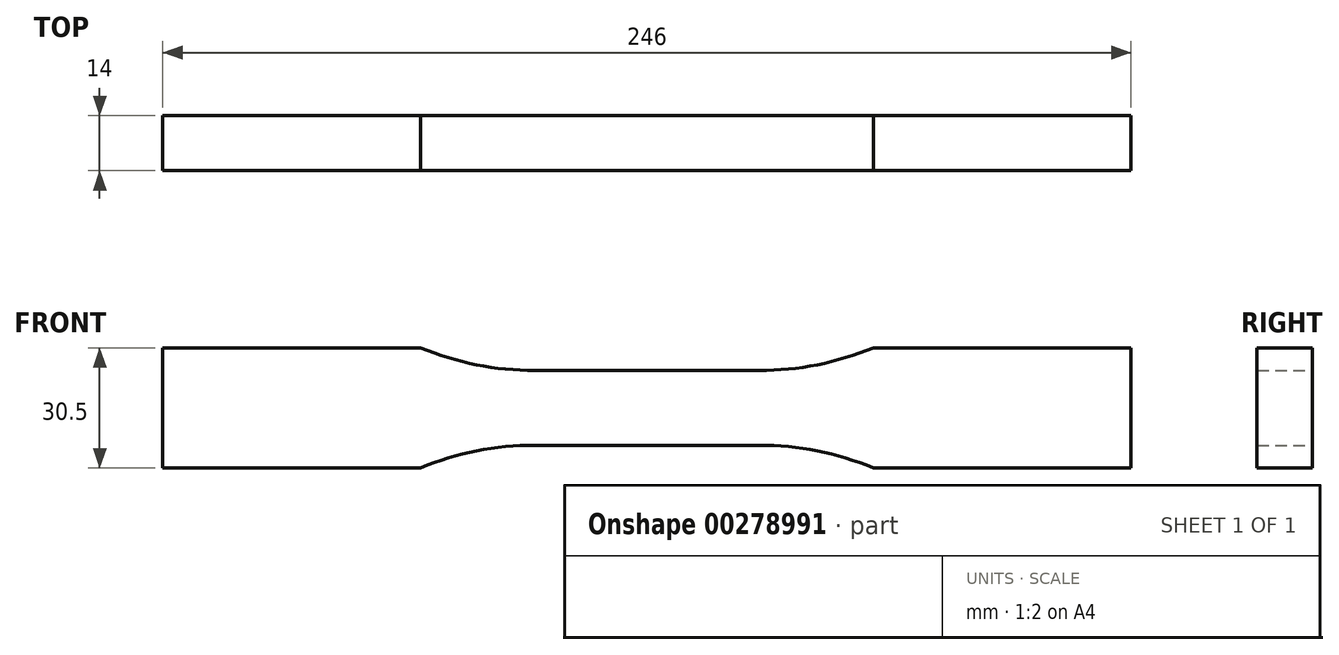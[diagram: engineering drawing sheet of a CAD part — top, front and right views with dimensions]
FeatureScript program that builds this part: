
annotation { "Feature Type Name" : "Feature", "Feature Type Description" : "" }
export const myFeature = defineFeature(function(context is Context, id is Id, definition is map)
    precondition{}
    {
        {
            var Q0;
            Q0=qCreatedBy(makeId("Front.planeOp"),FACE);
            var sketch = newSketch(context, id + "F0", { "sketchPlane" : qUnion([Q0])});
            skLineSegment(sketch, "E0", {"start": v(0, 9.5) * mm, "end": v(28.5, 9.5) * mm});
            skArc(sketch, "E1", {"start": v(28.5, 9.5) * mm, "mid": v(43.28, 10.95) * mm, "end": v(57.5, 15.25) * mm});
            skLineSegment(sketch, "E2", {"start": v(57.5, 15.25) * mm, "end": v(123, 15.25) * mm});
            skLineSegment(sketch, "E3.MirrorCS", {"start": v(-57.5, 15.25) * mm, "end": v(-123, 15.25) * mm});
            skLineSegment(sketch, "E4.MirrorCS", {"start": v(0, 9.5) * mm, "end": v(-28.5, 9.5) * mm});
            skArc(sketch, "E5.MirrorCS", {"start": v(-28.5, 9.5) * mm, "mid": v(-43.28, 10.95) * mm, "end": v(-57.5, 15.25) * mm});
            skArc(sketch, "E6.MirrorCS", {"start": v(-28.5, -9.5) * mm, "mid": v(-43.28, -10.95) * mm, "end": v(-57.5, -15.25) * mm});
            skLineSegment(sketch, "E7.MirrorCS", {"start": v(0, -9.5) * mm, "end": v(28.5, -9.5) * mm});
            skArc(sketch, "E8.MirrorCS", {"start": v(28.5, -9.5) * mm, "mid": v(43.28, -10.95) * mm, "end": v(57.5, -15.25) * mm});
            skLineSegment(sketch, "E9.MirrorCS", {"start": v(-57.5, -15.25) * mm, "end": v(-123, -15.25) * mm});
            skLineSegment(sketch, "E10.MirrorCS", {"start": v(0, -9.5) * mm, "end": v(-28.5, -9.5) * mm});
            skLineSegment(sketch, "E11.MirrorCS", {"start": v(57.5, -15.25) * mm, "end": v(123, -15.25) * mm});
            skLineSegment(sketch, "E12", {"start": v(-123, 15.25) * mm, "end": v(-123, -15.25) * mm});
            skLineSegment(sketch, "E13", {"start": v(123, 15.25) * mm, "end": v(123, -15.25) * mm});
            skSolve(sketch);
        }
        {
            var Q0;
            Q0=makeQuery(id+"F0.imprint","IMPRINT",FACE,{"disambiguationData":[TD([[makeQuery(id+"F0.imprint","IMPRINT",EDGE,{"derivedFrom":sQuery(id+"F0.wireOp",EDGE,"E0")}),-1.0]])]});
            extrude(context, id + "F1", {"entities" : qUnion([Q0]), "endBound" : BoundingType.SYMMETRIC, "depth" : 14 * mm});
        }
    });
